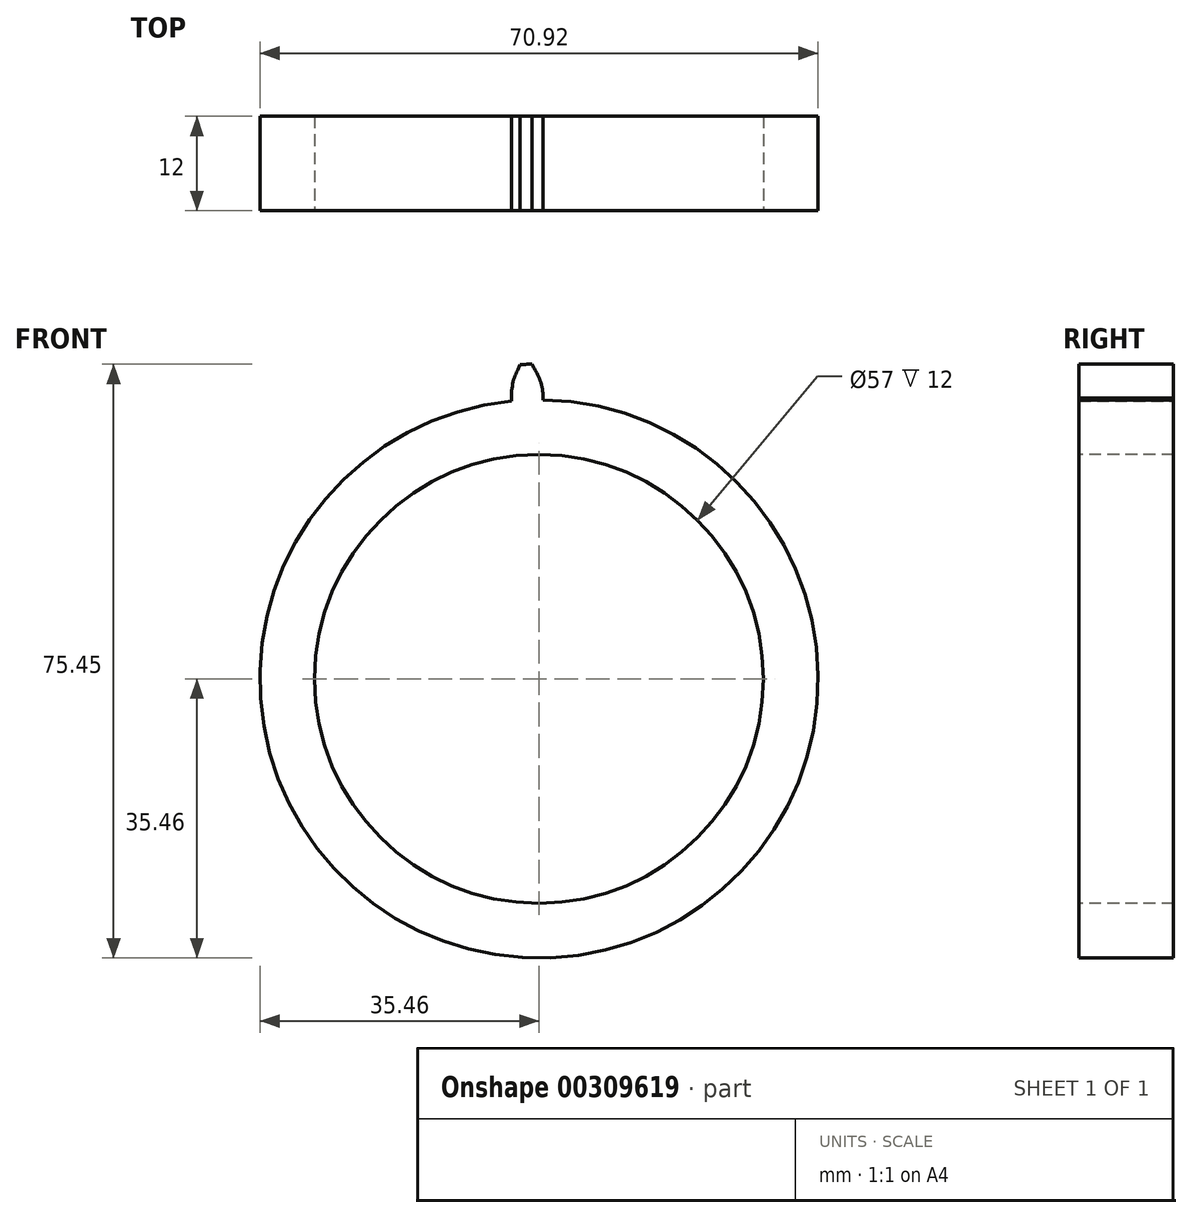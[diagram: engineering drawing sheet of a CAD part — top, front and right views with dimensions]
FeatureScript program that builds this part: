
annotation { "Feature Type Name" : "Feature", "Feature Type Description" : "" }
export const myFeature = defineFeature(function(context is Context, id is Id, definition is map)
    precondition{}
    {
        {
            var Q0;
            Q0=qCreatedBy(makeId("Front.planeOp"),FACE);
            var sketch = newSketch(context, id + "F0", { "sketchPlane" : qUnion([Q0])});
            skCircle(sketch, "E0", {"center": v(0, 0) * mm, "radius": 38 * mm, "construction": true});
            skLineSegment(sketch, "E1", {"start": v(0, 0) * mm, "end": v(0, 78.06) * mm, "construction": true});
            skLineSegment(sketch, "E2", {"start": v(-69.14, 38) * mm, "end": v(79.27, 38) * mm, "construction": true});
            skLineSegment(sketch, "E3", {"start": v(-72.02, 11.79) * mm, "end": v(65.8, 61.95) * mm, "construction": true});
            skPoint(sketch, "E4", {"position": v(0, 38) * mm});
            skLineSegment(sketch, "E5", {"start": v(0, 0) * mm, "end": v(-12.21, 33.55) * mm, "construction": true});
            skCircle(sketch, "E6", {"center": v(0, 0) * mm, "radius": 35.7 * mm, "construction": true});
            skArc(sketch, "E7", {"start": v(-12.21, 33.55) * mm, "mid": v(-14.76, 32.52) * mm, "end": v(-17.22, 31.28) * mm});
            skLineSegment(sketch, "E8", {"start": v(-17.22, 31.28) * mm, "end": v(-12.4, 33.94) * mm});
            skLineSegment(sketch, "E9", {"start": v(-12.21, 33.55) * mm, "end": v(0, 38) * mm});
            skLineSegment(sketch, "E10", {"start": v(0, 0) * mm, "end": v(-17.22, 31.28) * mm, "construction": true});
            skLineSegment(sketch, "E11", {"start": v(-12.4, 33.94) * mm, "end": v(-1.01, 40.2) * mm});
            skArc(sketch, "E12", {"start": v(-4.45, 35.43) * mm, "mid": v(-8.39, 34.7) * mm, "end": v(-12.21, 33.55) * mm});
            skLineSegment(sketch, "E13", {"start": v(-4.45, 35.43) * mm, "end": v(8.44, 37.05) * mm, "construction": true});
            skLineSegment(sketch, "E14", {"start": v(8.44, 37.05) * mm, "end": v(0.5, 36.05) * mm});
            skArc(sketch, "E15", {"start": v(0.53, 35.7) * mm, "mid": v(-5.94, 35.21) * mm, "end": v(-12.21, 33.55) * mm});
            skSolve(sketch);
        }
        {
            var Q0;
            Q0=qCreatedBy(makeId("Front.planeOp"),FACE);
            var sketch = newSketch(context, id + "F1", { "sketchPlane" : qUnion([Q0])});
            skPoint(sketch, "E16.0", {"position": v(-1.01, 40.2) * mm});
            skPoint(sketch, "E16.1", {"position": v(0, 38) * mm});
            skPoint(sketch, "E16.2", {"position": v(0.5, 36.05) * mm});
            skPoint(sketch, "E16.3", {"position": v(0.53, 35.7) * mm});
            skFitSpline(sketch, "E17", {"points": [v(-1.01, 40.2) * mm, v(0, 38) * mm, v(0.5, 36.05) * mm, v(0.53, 35.7) * mm], "startDerivative": vector(2.24, -4.38) * mm, "endDerivative": vector(0.02, -1.6) * mm});
            skLineSegment(sketch, "E18", {"start": v(0, 0) * mm, "end": v(-2, 48.22) * mm, "construction": true});
            skFitSpline(sketch, "E19.MirrorCS", {"points": [v(-2.31, 40.15) * mm, v(-3.14, 37.87) * mm, v(-3.48, 35.89) * mm, v(-3.48, 35.54) * mm], "startDerivative": vector(-1.87, -4.55) * mm, "endDerivative": vector(0.1, -1.6) * mm});
            skCircle(sketch, "E20", {"center": v(0, 0) * mm, "radius": 40 * mm});
            skSolve(sketch);
        }
        {
            var Q0;
            Q0=qCreatedBy(makeId("Front.planeOp"),FACE);
            var sketch = newSketch(context, id + "F2", { "sketchPlane" : qUnion([Q0])});
            skFitSpline(sketch, "E21.0", {"points": [v(-1.01, 40.2) * mm, v(-0.69, 39.56) * mm, v(0.07, 38.14) * mm, v(0.52, 36.11) * mm, v(0.53, 35.8) * mm, v(0.53, 35.7) * mm]});
            skArc(sketch, "E21.1", {"start": v(-0.9, 39.99) * mm, "mid": v(-1.65, 39.97) * mm, "end": v(-2.4, 39.93) * mm});
            skFitSpline(sketch, "E21.2", {"points": [v(-2.31, 40.15) * mm, v(-2.58, 39.49) * mm, v(-3.22, 38) * mm, v(-3.5, 35.95) * mm, v(-3.49, 35.63) * mm, v(-3.48, 35.54) * mm]});
            skPoint(sketch, "E22.orphan", {"position": v(-1.01, 40.2) * mm});
            skPoint(sketch, "E23.orphan", {"position": v(-2.31, 40.15) * mm});
            skLineSegment(sketch, "E24", {"start": v(0.53, 35.7) * mm, "end": v(0.54, 35.45) * mm});
            skLineSegment(sketch, "E25", {"start": v(-3.47, 35.29) * mm, "end": v(-3.48, 35.54) * mm});
            skArc(sketch, "E26", {"start": v(0.54, 35.45) * mm, "mid": v(-1.47, 35.43) * mm, "end": v(-3.47, 35.29) * mm});
            skCircle(sketch, "E27", {"center": v(0, 0) * mm, "radius": 35.46 * mm, "construction": true});
            skSolve(sketch);
        }
        {
            var Q0;
            Q0=qCreatedBy(makeId("Front.planeOp"),FACE);
            var sketch = newSketch(context, id + "F3", { "sketchPlane" : qUnion([Q0])});
            skCircle(sketch, "E28.0", {"center": v(0, 0) * mm, "radius": 35.46 * mm});
            skSolve(sketch);
        }
        {
            var Q0;
            Q0 = qSketchRegion(id + "F3", true);
            extrude(context, id + "F4", {"entities" : qUnion([Q0]), "depth" : 12 * mm});
        }
        {
            var Q0;
            Q0=qCreatedBy(makeId("Front.planeOp"),FACE);
            var sketch = newSketch(context, id + "F5", { "sketchPlane" : qUnion([Q0])});
            skArc(sketch, "E29.0", {"start": v(0.54, 35.45) * mm, "mid": v(-1.47, 35.43) * mm, "end": v(-3.47, 35.29) * mm});
            skLineSegment(sketch, "E29.1", {"start": v(0.53, 35.7) * mm, "end": v(0.54, 35.45) * mm});
            skFitSpline(sketch, "E29.2", {"points": [v(-1.01, 40.2) * mm, v(-0.69, 39.56) * mm, v(0.07, 38.14) * mm, v(0.52, 36.11) * mm, v(0.53, 35.8) * mm, v(0.53, 35.7) * mm]});
            skArc(sketch, "E29.3", {"start": v(-0.9, 39.99) * mm, "mid": v(-1.65, 39.97) * mm, "end": v(-2.4, 39.93) * mm});
            skFitSpline(sketch, "E29.4", {"points": [v(-2.31, 40.15) * mm, v(-2.58, 39.49) * mm, v(-3.22, 38) * mm, v(-3.5, 35.95) * mm, v(-3.49, 35.63) * mm, v(-3.48, 35.54) * mm]});
            skLineSegment(sketch, "E29.5", {"start": v(-3.47, 35.29) * mm, "end": v(-3.48, 35.54) * mm});
            skSolve(sketch);
        }
        {
            var Q0;
            Q0 = qSketchRegion(id + "F5", true);
            var Q1;
            Q1=makeQuery(id+"F4.opExtrude","CAP_FACE",FACE,{"disambiguationData":[OSD([sQuery(id+"F3.wireOp",EDGE,"E28.0")])],"isStart":false});
            extrude(context, id + "F6", {"entities" : qUnion([Q0]), "operationType" : NewBodyOperationType.ADD, "endBound" : BoundingType.UP_TO_SURFACE, "endBoundEntityFace" : qUnion([Q1]), "depth" : 25 * mm});
        }
        {
            var Q0;
            {var subQ0=sQuery(id+"F3.wireOp",EDGE,"E28.0");Q0=makeQuery(id+"FfI0IxFe3YmUk1V_1.37.F6.boolean.opBoolean","MERGE",FACE,{"derivedFrom":[makeQuery(id+"FfI0IxFe3YmUk1V_1.36.F6.boolean.opBoolean","MERGE",FACE,{"derivedFrom":[makeQuery(id+"FfI0IxFe3YmUk1V_1.35.F6.boolean.opBoolean","MERGE",FACE,{"derivedFrom":[makeQuery(id+"FfI0IxFe3YmUk1V_1.34.F6.boolean.opBoolean","MERGE",FACE,{"derivedFrom":[makeQuery(id+"FfI0IxFe3YmUk1V_1.33.F6.boolean.opBoolean","MERGE",FACE,{"derivedFrom":[makeQuery(id+"FfI0IxFe3YmUk1V_1.32.F6.boolean.opBoolean","MERGE",FACE,{"derivedFrom":[makeQuery(id+"FfI0IxFe3YmUk1V_1.31.F6.boolean.opBoolean","MERGE",FACE,{"derivedFrom":[makeQuery(id+"FfI0IxFe3YmUk1V_1.30.F6.boolean.opBoolean","MERGE",FACE,{"derivedFrom":[makeQuery(id+"FfI0IxFe3YmUk1V_1.29.F6.boolean.opBoolean","MERGE",FACE,{"derivedFrom":[makeQuery(id+"FfI0IxFe3YmUk1V_1.28.F6.boolean.opBoolean","MERGE",FACE,{"derivedFrom":[makeQuery(id+"FfI0IxFe3YmUk1V_1.27.F6.boolean.opBoolean","MERGE",FACE,{"derivedFrom":[makeQuery(id+"FfI0IxFe3YmUk1V_1.26.F6.boolean.opBoolean","MERGE",FACE,{"derivedFrom":[makeQuery(id+"FfI0IxFe3YmUk1V_1.25.F6.boolean.opBoolean","MERGE",FACE,{"derivedFrom":[makeQuery(id+"FfI0IxFe3YmUk1V_1.24.F6.boolean.opBoolean","MERGE",FACE,{"derivedFrom":[makeQuery(id+"FfI0IxFe3YmUk1V_1.23.F6.boolean.opBoolean","MERGE",FACE,{"derivedFrom":[makeQuery(id+"FfI0IxFe3YmUk1V_1.22.F6.boolean.opBoolean","MERGE",FACE,{"derivedFrom":[makeQuery(id+"FfI0IxFe3YmUk1V_1.21.F6.boolean.opBoolean","MERGE",FACE,{"derivedFrom":[makeQuery(id+"FfI0IxFe3YmUk1V_1.20.F6.boolean.opBoolean","MERGE",FACE,{"derivedFrom":[makeQuery(id+"FfI0IxFe3YmUk1V_1.19.F6.boolean.opBoolean","MERGE",FACE,{"derivedFrom":[makeQuery(id+"FfI0IxFe3YmUk1V_1.18.F6.boolean.opBoolean","MERGE",FACE,{"derivedFrom":[makeQuery(id+"FfI0IxFe3YmUk1V_1.17.F6.boolean.opBoolean","MERGE",FACE,{"derivedFrom":[makeQuery(id+"FfI0IxFe3YmUk1V_1.16.F6.boolean.opBoolean","MERGE",FACE,{"derivedFrom":[makeQuery(id+"FfI0IxFe3YmUk1V_1.15.F6.boolean.opBoolean","MERGE",FACE,{"derivedFrom":[makeQuery(id+"FfI0IxFe3YmUk1V_1.14.F6.boolean.opBoolean","MERGE",FACE,{"derivedFrom":[makeQuery(id+"FfI0IxFe3YmUk1V_1.13.F6.boolean.opBoolean","MERGE",FACE,{"derivedFrom":[makeQuery(id+"FfI0IxFe3YmUk1V_1.12.F6.boolean.opBoolean","MERGE",FACE,{"derivedFrom":[makeQuery(id+"FfI0IxFe3YmUk1V_1.11.F6.boolean.opBoolean","MERGE",FACE,{"derivedFrom":[makeQuery(id+"FfI0IxFe3YmUk1V_1.10.F6.boolean.opBoolean","MERGE",FACE,{"derivedFrom":[makeQuery(id+"FfI0IxFe3YmUk1V_1.9.F6.boolean.opBoolean","MERGE",FACE,{"derivedFrom":[makeQuery(id+"FfI0IxFe3YmUk1V_1.8.F6.boolean.opBoolean","MERGE",FACE,{"derivedFrom":[makeQuery(id+"FfI0IxFe3YmUk1V_1.7.F6.boolean.opBoolean","MERGE",FACE,{"derivedFrom":[makeQuery(id+"FfI0IxFe3YmUk1V_1.6.F6.boolean.opBoolean","MERGE",FACE,{"derivedFrom":[makeQuery(id+"FfI0IxFe3YmUk1V_1.5.F6.boolean.opBoolean","MERGE",FACE,{"derivedFrom":[makeQuery(id+"FfI0IxFe3YmUk1V_1.4.F6.boolean.opBoolean","MERGE",FACE,{"derivedFrom":[makeQuery(id+"FfI0IxFe3YmUk1V_1.3.F6.boolean.opBoolean","MERGE",FACE,{"derivedFrom":[makeQuery(id+"FfI0IxFe3YmUk1V_1.2.F6.boolean.opBoolean","MERGE",FACE,{"derivedFrom":[makeQuery(id+"FfI0IxFe3YmUk1V_1.1.F6.boolean.opBoolean","MERGE",FACE,{"derivedFrom":[makeQuery(id+"F6.boolean.opBoolean","MERGE",FACE,{"derivedFrom":[makeQuery(id+"F4.opExtrude","CAP_FACE",FACE,{"disambiguationData":[OSD([subQ0])],"isStart":false}),makeQuery(id+"F6.opExtrude","CAP_FACE",FACE,{"disambiguationData":[OSD([subQ0])],"isStart":false})]}),makeQuery(id+"FfI0IxFe3YmUk1V_1.1.F6.opExtrude","CAP_FACE",FACE,{"disambiguationData":[OSD([subQ0])],"isStart":false})]}),makeQuery(id+"FfI0IxFe3YmUk1V_1.2.F6.opExtrude","CAP_FACE",FACE,{"disambiguationData":[OSD([subQ0])],"isStart":false})]}),makeQuery(id+"FfI0IxFe3YmUk1V_1.3.F6.opExtrude","CAP_FACE",FACE,{"disambiguationData":[OSD([subQ0])],"isStart":false})]}),makeQuery(id+"FfI0IxFe3YmUk1V_1.4.F6.opExtrude","CAP_FACE",FACE,{"disambiguationData":[OSD([subQ0])],"isStart":false})]}),makeQuery(id+"FfI0IxFe3YmUk1V_1.5.F6.opExtrude","CAP_FACE",FACE,{"disambiguationData":[OSD([subQ0])],"isStart":false})]}),makeQuery(id+"FfI0IxFe3YmUk1V_1.6.F6.opExtrude","CAP_FACE",FACE,{"disambiguationData":[OSD([subQ0])],"isStart":false})]}),makeQuery(id+"FfI0IxFe3YmUk1V_1.7.F6.opExtrude","CAP_FACE",FACE,{"disambiguationData":[OSD([subQ0])],"isStart":false})]}),makeQuery(id+"FfI0IxFe3YmUk1V_1.8.F6.opExtrude","CAP_FACE",FACE,{"disambiguationData":[OSD([subQ0])],"isStart":false})]}),makeQuery(id+"FfI0IxFe3YmUk1V_1.9.F6.opExtrude","CAP_FACE",FACE,{"disambiguationData":[OSD([subQ0])],"isStart":false})]}),makeQuery(id+"FfI0IxFe3YmUk1V_1.10.F6.opExtrude","CAP_FACE",FACE,{"disambiguationData":[OSD([subQ0])],"isStart":false})]}),makeQuery(id+"FfI0IxFe3YmUk1V_1.11.F6.opExtrude","CAP_FACE",FACE,{"disambiguationData":[OSD([subQ0])],"isStart":false})]}),makeQuery(id+"FfI0IxFe3YmUk1V_1.12.F6.opExtrude","CAP_FACE",FACE,{"disambiguationData":[OSD([subQ0])],"isStart":false})]}),makeQuery(id+"FfI0IxFe3YmUk1V_1.13.F6.opExtrude","CAP_FACE",FACE,{"disambiguationData":[OSD([subQ0])],"isStart":false})]}),makeQuery(id+"FfI0IxFe3YmUk1V_1.14.F6.opExtrude","CAP_FACE",FACE,{"disambiguationData":[OSD([subQ0])],"isStart":false})]}),makeQuery(id+"FfI0IxFe3YmUk1V_1.15.F6.opExtrude","CAP_FACE",FACE,{"disambiguationData":[OSD([subQ0])],"isStart":false})]}),makeQuery(id+"FfI0IxFe3YmUk1V_1.16.F6.opExtrude","CAP_FACE",FACE,{"disambiguationData":[OSD([subQ0])],"isStart":false})]}),makeQuery(id+"FfI0IxFe3YmUk1V_1.17.F6.opExtrude","CAP_FACE",FACE,{"disambiguationData":[OSD([subQ0])],"isStart":false})]}),makeQuery(id+"FfI0IxFe3YmUk1V_1.18.F6.opExtrude","CAP_FACE",FACE,{"disambiguationData":[OSD([subQ0])],"isStart":false})]}),makeQuery(id+"FfI0IxFe3YmUk1V_1.19.F6.opExtrude","CAP_FACE",FACE,{"disambiguationData":[OSD([subQ0])],"isStart":false})]}),makeQuery(id+"FfI0IxFe3YmUk1V_1.20.F6.opExtrude","CAP_FACE",FACE,{"disambiguationData":[OSD([subQ0])],"isStart":false})]}),makeQuery(id+"FfI0IxFe3YmUk1V_1.21.F6.opExtrude","CAP_FACE",FACE,{"disambiguationData":[OSD([subQ0])],"isStart":false})]}),makeQuery(id+"FfI0IxFe3YmUk1V_1.22.F6.opExtrude","CAP_FACE",FACE,{"disambiguationData":[OSD([subQ0])],"isStart":false})]}),makeQuery(id+"FfI0IxFe3YmUk1V_1.23.F6.opExtrude","CAP_FACE",FACE,{"disambiguationData":[OSD([subQ0])],"isStart":false})]}),makeQuery(id+"FfI0IxFe3YmUk1V_1.24.F6.opExtrude","CAP_FACE",FACE,{"disambiguationData":[OSD([subQ0])],"isStart":false})]}),makeQuery(id+"FfI0IxFe3YmUk1V_1.25.F6.opExtrude","CAP_FACE",FACE,{"disambiguationData":[OSD([subQ0])],"isStart":false})]}),makeQuery(id+"FfI0IxFe3YmUk1V_1.26.F6.opExtrude","CAP_FACE",FACE,{"disambiguationData":[OSD([subQ0])],"isStart":false})]}),makeQuery(id+"FfI0IxFe3YmUk1V_1.27.F6.opExtrude","CAP_FACE",FACE,{"disambiguationData":[OSD([subQ0])],"isStart":false})]}),makeQuery(id+"FfI0IxFe3YmUk1V_1.28.F6.opExtrude","CAP_FACE",FACE,{"disambiguationData":[OSD([subQ0])],"isStart":false})]}),makeQuery(id+"FfI0IxFe3YmUk1V_1.29.F6.opExtrude","CAP_FACE",FACE,{"disambiguationData":[OSD([subQ0])],"isStart":false})]}),makeQuery(id+"FfI0IxFe3YmUk1V_1.30.F6.opExtrude","CAP_FACE",FACE,{"disambiguationData":[OSD([subQ0])],"isStart":false})]}),makeQuery(id+"FfI0IxFe3YmUk1V_1.31.F6.opExtrude","CAP_FACE",FACE,{"disambiguationData":[OSD([subQ0])],"isStart":false})]}),makeQuery(id+"FfI0IxFe3YmUk1V_1.32.F6.opExtrude","CAP_FACE",FACE,{"disambiguationData":[OSD([subQ0])],"isStart":false})]}),makeQuery(id+"FfI0IxFe3YmUk1V_1.33.F6.opExtrude","CAP_FACE",FACE,{"disambiguationData":[OSD([subQ0])],"isStart":false})]}),makeQuery(id+"FfI0IxFe3YmUk1V_1.34.F6.opExtrude","CAP_FACE",FACE,{"disambiguationData":[OSD([subQ0])],"isStart":false})]}),makeQuery(id+"FfI0IxFe3YmUk1V_1.35.F6.opExtrude","CAP_FACE",FACE,{"disambiguationData":[OSD([subQ0])],"isStart":false})]}),makeQuery(id+"FfI0IxFe3YmUk1V_1.36.F6.opExtrude","CAP_FACE",FACE,{"disambiguationData":[OSD([subQ0])],"isStart":false})]}),makeQuery(id+"FfI0IxFe3YmUk1V_1.37.F6.opExtrude","CAP_FACE",FACE,{"disambiguationData":[OSD([subQ0])],"isStart":false})]});}
            var sketch = newSketch(context, id + "F7", { "sketchPlane" : qUnion([Q0])});
            skCircle(sketch, "E30", {"center": v(0, 0) * mm, "radius": 28.5 * mm});
            skSolve(sketch);
        }
        {
            var Q0;
            Q0 = qSketchRegion(id + "F7", true);
            extrude(context, id + "F8", {"entities" : qUnion([Q0]), "operationType" : NewBodyOperationType.REMOVE, "endBound" : BoundingType.THROUGH_ALL, "oppositeDirection" : true, "depth" : 25 * mm});
        }
    });
